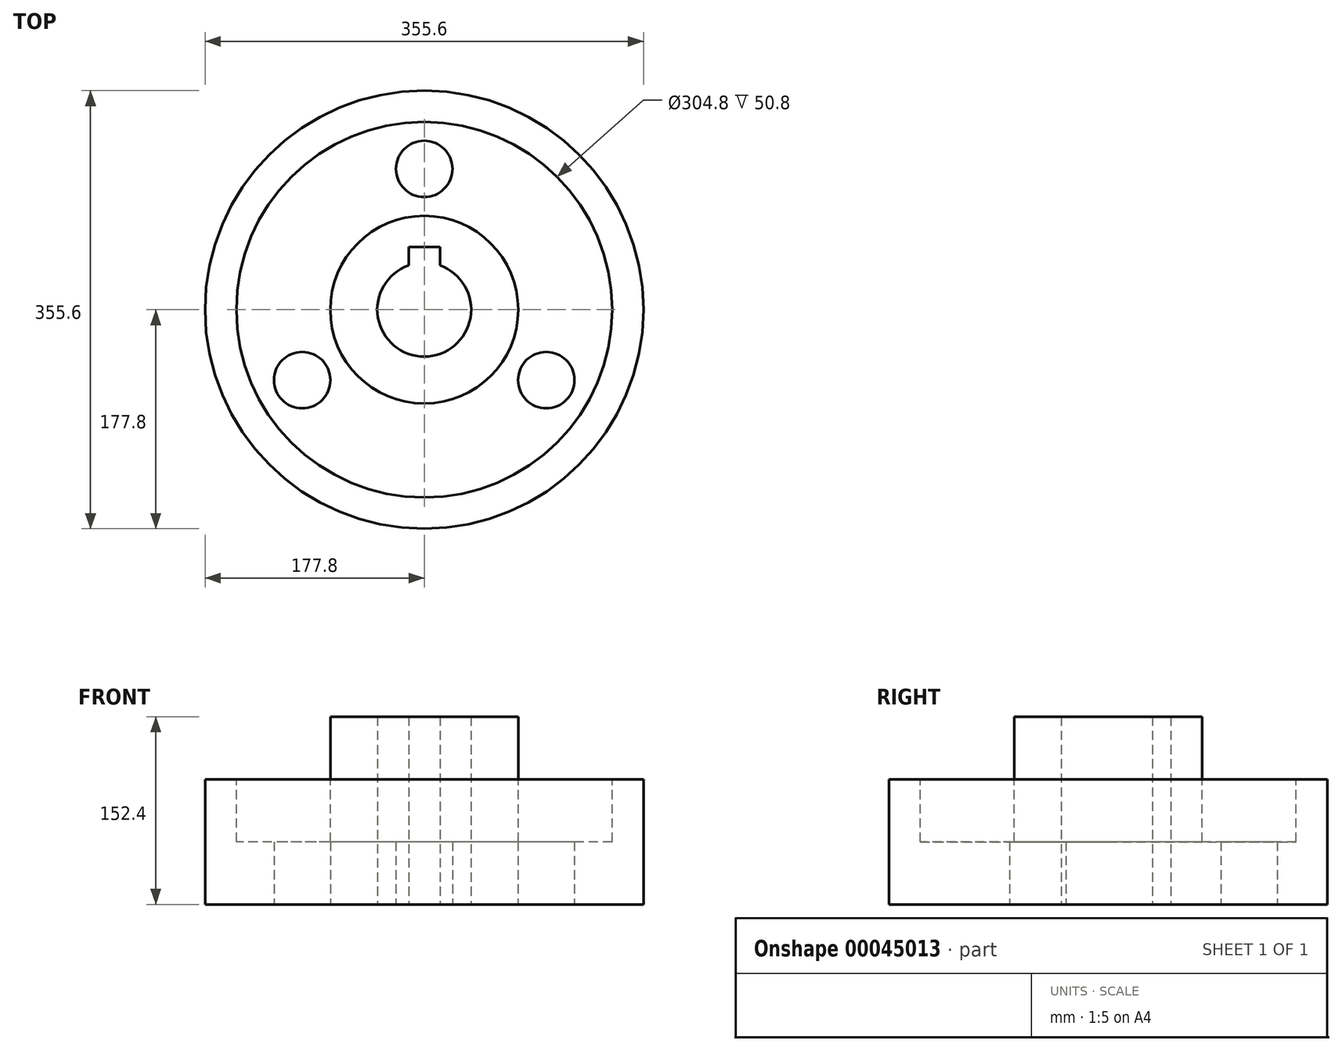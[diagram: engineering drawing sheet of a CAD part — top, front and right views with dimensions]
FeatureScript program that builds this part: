
annotation { "Feature Type Name" : "Feature", "Feature Type Description" : "" }
export const myFeature = defineFeature(function(context is Context, id is Id, definition is map)
    precondition{}
    {
        {
            var Q0;
            Q0=qCreatedBy(makeId("Top.planeOp"),FACE);
            var sketch = newSketch(context, id + "F0", { "sketchPlane" : qUnion([Q0])});
            skCircle(sketch, "E0", {"center": v(0, 0) * mm, "radius": 177.8 * mm});
            skCircle(sketch, "E1", {"center": v(0, 0) * mm, "radius": 38.1 * mm});
            skLineSegment(sketch, "E2.rect.bottom", {"start": v(-12.7, 50.8) * mm, "end": v(12.7, 50.8) * mm});
            skLineSegment(sketch, "E2.rect.top", {"start": v(-12.7, 25.4) * mm, "end": v(12.7, 25.4) * mm});
            skLineSegment(sketch, "E2.rect.left", {"start": v(-12.7, 50.8) * mm, "end": v(-12.7, 25.4) * mm});
            skLineSegment(sketch, "E2.rect.right", {"start": v(12.7, 50.8) * mm, "end": v(12.7, 25.4) * mm});
            skPoint(sketch, "E2.rect.middle", {"position": v(0, 38.1) * mm});
            skCircle(sketch, "E3", {"center": v(0, 0) * mm, "radius": 114.3 * mm, "construction": true});
            skCircle(sketch, "E4", {"center": v(0, 114.3) * mm, "radius": 22.86 * mm});
            skPoint(sketch, "E4.centerSnap0", {"position": v(0, 50.8) * mm});
            skCircle(sketch, "E5.1.0", {"center": v(-98.99, -57.15) * mm, "radius": 22.86 * mm});
            skCircle(sketch, "E5.2.0", {"center": v(98.99, -57.15) * mm, "radius": 22.86 * mm});
            skSolve(sketch);
        }
        {
            var Q0;
            Q0 = qSketchRegion(id + "F0", true);
            extrude(context, id + "F1", {"entities" : qUnion([Q0]), "depth" : 152.4 * mm});
        }
        {
            var Q0;
            Q0=makeQuery(id+"F1.opExtrude","CAP_FACE",FACE,{"disambiguationData":[OSD([sQuery(id+"F0.wireOp",EDGE,"E0"),sQuery(id+"F0.wireOp",EDGE,"E1"),sQuery(id+"F0.wireOp",EDGE,"E2.rect.bottom"),sQuery(id+"F0.wireOp",EDGE,"E2.rect.left"),sQuery(id+"F0.wireOp",EDGE,"E2.rect.right"),sQuery(id+"F0.wireOp",EDGE,"E4"),sQuery(id+"F0.wireOp",EDGE,"E5.1.0"),sQuery(id+"F0.wireOp",EDGE,"E5.2.0")])],"isStart":false});
            var sketch = newSketch(context, id + "F2", { "sketchPlane" : qUnion([Q0])});
            skCircle(sketch, "E6", {"center": v(0, 0) * mm, "radius": 76.2 * mm});
            skCircle(sketch, "E7", {"center": v(0, 0) * mm, "radius": 152.4 * mm});
            skSolve(sketch);
        }
        {
            var Q0;
            Q0 = qSketchRegion(id + "F2", true);
            extrude(context, id + "F3", {"entities" : qUnion([Q0]), "operationType" : NewBodyOperationType.REMOVE, "oppositeDirection" : true, "depth" : 101.6 * mm});
        }
        {
            var Q0;
            {var subQ0=sQuery(id+"F0.wireOp",EDGE,"E0");Q0=makeQuery(id+"F3.boolean.opBoolean","SPLIT",FACE,{"disambiguationData":[TD([makeQuery(id+"F1.opExtrude","SWEPT_FACE",FACE,{"disambiguationData":[OSD([subQ0])]})])],"derivedFrom":makeQuery(id+"F1.opExtrude","CAP_FACE",FACE,{"disambiguationData":[OSD([subQ0,sQuery(id+"F0.wireOp",EDGE,"E1"),sQuery(id+"F0.wireOp",EDGE,"E2.rect.bottom"),sQuery(id+"F0.wireOp",EDGE,"E2.rect.left"),sQuery(id+"F0.wireOp",EDGE,"E2.rect.right"),sQuery(id+"F0.wireOp",EDGE,"E4"),sQuery(id+"F0.wireOp",EDGE,"E5.1.0"),sQuery(id+"F0.wireOp",EDGE,"E5.2.0")])],"isStart":false})});}
            var sketch = newSketch(context, id + "F4", { "sketchPlane" : qUnion([Q0])});
            skCircle(sketch, "E8.0", {"center": v(0, 0) * mm, "radius": 152.4 * mm});
            skCircle(sketch, "E8.1", {"center": v(0, 0) * mm, "radius": 177.8 * mm});
            skSolve(sketch);
        }
        {
            var Q0;
            Q0=makeQuery(id+"F4.imprint","IMPRINT",FACE,{"disambiguationData":[TD([[makeQuery(id+"F4.imprint","IMPRINT",EDGE,{"derivedFrom":sQuery(id+"F4.wireOp",EDGE,"E8.0")}),-1.0]])]});
            extrude(context, id + "F5", {"entities" : qUnion([Q0]), "operationType" : NewBodyOperationType.REMOVE, "oppositeDirection" : true, "depth" : 50.8 * mm});
        }
    });
